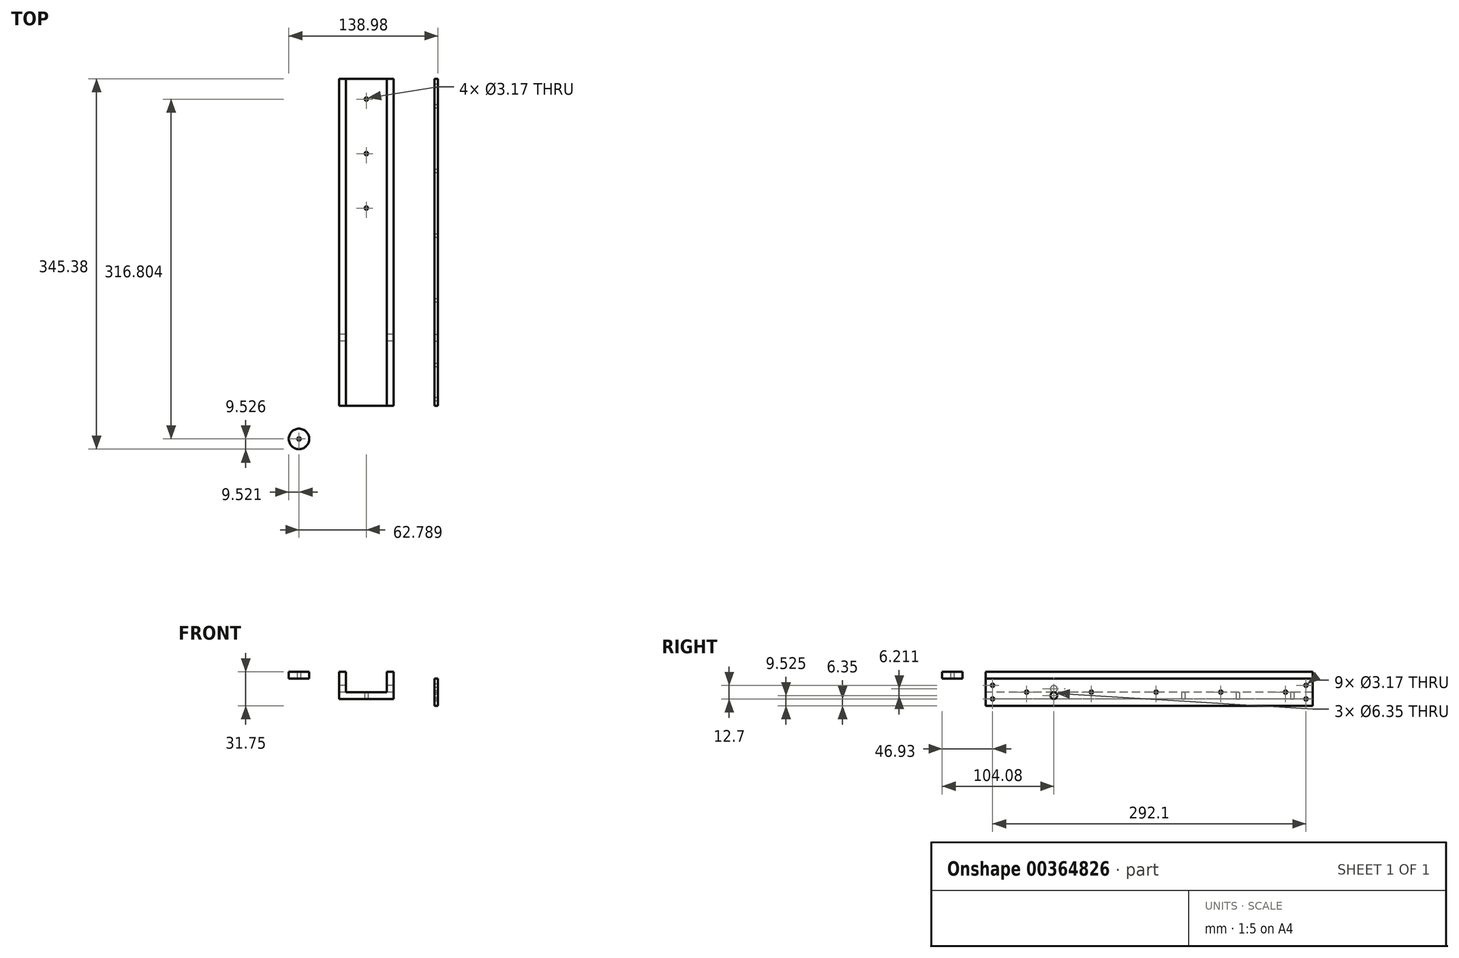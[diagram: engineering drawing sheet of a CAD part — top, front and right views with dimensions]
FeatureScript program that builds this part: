
annotation { "Feature Type Name" : "Feature", "Feature Type Description" : "" }
export const myFeature = defineFeature(function(context is Context, id is Id, definition is map)
    precondition{}
    {
        {
            var Q0;
            Q0=qCreatedBy(makeId("Front.planeOp"),FACE);
            var sketch = newSketch(context, id + "F0", { "sketchPlane" : qUnion([Q0])});
            skLineSegment(sketch, "E0", {"start": v(-25.4, 6.21) * mm, "end": v(-25.4, -19.19) * mm});
            skLineSegment(sketch, "E1", {"start": v(-25.4, -19.19) * mm, "end": v(25.4, -19.19) * mm});
            skLineSegment(sketch, "E2", {"start": v(25.4, -19.19) * mm, "end": v(25.4, 6.21) * mm});
            skLineSegment(sketch, "E3", {"start": v(25.4, 6.21) * mm, "end": v(19.05, 6.21) * mm});
            skLineSegment(sketch, "E4", {"start": v(19.05, 6.21) * mm, "end": v(19.05, -12.84) * mm});
            skLineSegment(sketch, "E5", {"start": v(19.05, -12.84) * mm, "end": v(-19.05, -12.84) * mm});
            skLineSegment(sketch, "E6", {"start": v(-19.05, -12.84) * mm, "end": v(-19.05, 6.21) * mm});
            skLineSegment(sketch, "E7", {"start": v(-19.05, 6.21) * mm, "end": v(-25.4, 6.21) * mm});
            skSolve(sketch);
        }
        {
            var Q0;
            Q0 = qSketchRegion(id + "F0", true);
            extrude(context, id + "F1", {"entities" : qUnion([Q0]), "oppositeDirection" : true, "depth" : 304.8 * mm, "offsetDistance" : 25.4 * mm});
        }
        {
            var Q0;
            Q0=makeQuery(id+"F1.opExtrude","SWEPT_FACE",FACE,{"disambiguationData":[OSD([sQuery(id+"F0.wireOp",EDGE,"E0")])]});
            var sketch = newSketch(context, id + "F2", { "sketchPlane" : qUnion([Q0])});
            skLineSegment(sketch, "E8", {"start": v(2.62, -9.66) * mm, "end": v(-42.46, -9.66) * mm, "construction": true});
            skLineSegment(sketch, "E9", {"start": v(-63.5, -22.2) * mm, "end": v(-63.5, -9.66) * mm, "construction": true});
            skCircle(sketch, "E10", {"center": v(-63.5, -9.66) * mm, "radius": 3.18 * mm});
            skSolve(sketch);
        }
        {
            var Q0;
            Q0 = qSketchRegion(id + "F2", true);
            var Q1;
            Q1=makeQuery(id+"F1.opExtrude","SWEPT_FACE",FACE,{"disambiguationData":[OSD([sQuery(id+"F0.wireOp",EDGE,"E2")])]});
            extrude(context, id + "F3", {"entities" : qUnion([Q0]), "operationType" : NewBodyOperationType.REMOVE, "endBound" : BoundingType.UP_TO_SURFACE, "oppositeDirection" : true, "depth" : 25.4 * mm, "endBoundEntityFace" : qUnion([Q1]), "offsetDistance" : 25.4 * mm});
        }
        {
            var Q0;
            Q0=qCreatedBy(makeId("Top.planeOp"),FACE);
            var sketch = newSketch(context, id + "F4", { "sketchPlane" : qUnion([Q0])});
            skLineSegment(sketch, "E11.bottom", {"start": v(63.5, 0) * mm, "end": v(66.67, 0) * mm});
            skLineSegment(sketch, "E11.top", {"start": v(63.5, 304.8) * mm, "end": v(66.67, 304.8) * mm});
            skLineSegment(sketch, "E11.left", {"start": v(63.5, 0) * mm, "end": v(63.5, 304.8) * mm});
            skLineSegment(sketch, "E11.right", {"start": v(66.67, 0) * mm, "end": v(66.67, 304.8) * mm});
            skSolve(sketch);
        }
        {
            var Q0;
            Q0 = qSketchRegion(id + "F4", true);
            extrude(context, id + "F5", {"entities" : qUnion([Q0]), "oppositeDirection" : true, "depth" : 25.4 * mm, "offsetDistance" : 25.4 * mm});
        }
        {
            var Q0;
            Q0=makeQuery(id+"F5.opExtrude","SWEPT_FACE",FACE,{"disambiguationData":[OSD([sQuery(id+"F4.wireOp",EDGE,"E11.right")])]});
            var sketch = newSketch(context, id + "F6", { "sketchPlane" : qUnion([Q0])});
            skLineSegment(sketch, "E12", {"start": v(-0.34, -15.88) * mm, "end": v(74.66, -15.87) * mm, "construction": true});
            skLineSegment(sketch, "E13", {"start": v(63.5, -28.22) * mm, "end": v(63.5, -15.87) * mm, "construction": true});
            skCircle(sketch, "E14", {"center": v(63.5, -15.87) * mm, "radius": 3.18 * mm});
            skSolve(sketch);
        }
        {
            var Q0;
            Q0 = qSketchRegion(id + "F6", true);
            extrude(context, id + "F7", {"entities" : qUnion([Q0]), "operationType" : NewBodyOperationType.REMOVE, "oppositeDirection" : true, "depth" : 25.4 * mm, "offsetDistance" : 25.4 * mm});
        }
        {
            var Q0;
            Q0=makeQuery(id+"F5.opExtrude","SWEPT_FACE",FACE,{"disambiguationData":[OSD([sQuery(id+"F4.wireOp",EDGE,"E11.right")])]});
            var sketch = newSketch(context, id + "F8", { "sketchPlane" : qUnion([Q0])});
            skLineSegment(sketch, "E15", {"start": v(-6.26, -12.7) * mm, "end": v(309.85, -12.7) * mm, "construction": true});
            skPoint(sketch, "E15.startSnap0", {"position": v(0, -12.7) * mm});
            skLineSegment(sketch, "E16", {"start": v(298.45, -28.77) * mm, "end": v(298.45, 10.49) * mm, "construction": true});
            skLineSegment(sketch, "E17", {"start": v(6.35, -30.25) * mm, "end": v(6.35, 2.85) * mm, "construction": true});
            skLineSegment(sketch, "E18", {"start": v(-5.59, -6.35) * mm, "end": v(6.35, -6.35) * mm, "construction": true});
            skLineSegment(sketch, "E19", {"start": v(-6.94, -19.05) * mm, "end": v(6.35, -19.05) * mm, "construction": true});
            skLineSegment(sketch, "E20", {"start": v(298.45, -6.35) * mm, "end": v(311.24, -6.35) * mm, "construction": true});
            skLineSegment(sketch, "E21", {"start": v(298.45, -19.05) * mm, "end": v(309.9, -19.05) * mm, "construction": true});
            skLineSegment(sketch, "E22", {"start": v(38.1, -3.72) * mm, "end": v(38.1, -12.7) * mm, "construction": true});
            skLineSegment(sketch, "E23", {"start": v(279.4, -4.06) * mm, "end": v(279.4, -12.7) * mm, "construction": true});
            skLineSegment(sketch, "E24", {"start": v(98.43, -4.74) * mm, "end": v(98.43, -12.7) * mm, "construction": true});
            skLineSegment(sketch, "E25", {"start": v(158.75, -6.6) * mm, "end": v(158.75, -12.7) * mm, "construction": true});
            skLineSegment(sketch, "E26", {"start": v(219.07, -5.25) * mm, "end": v(219.07, -12.7) * mm, "construction": true});
            skPoint(sketch, "E27.orphan", {"position": v(15.82, -6.35) * mm});
            skPoint(sketch, "E28.orphan", {"position": v(15.82, -19.05) * mm});
            skPoint(sketch, "E29.orphan", {"position": v(283.42, -6.35) * mm});
            skPoint(sketch, "E30.orphan", {"position": v(282.58, -19.05) * mm});
            skPoint(sketch, "E31.orphan", {"position": v(279.4, -21.15) * mm});
            skPoint(sketch, "E32.orphan", {"position": v(219.07, -19.12) * mm});
            skPoint(sketch, "E33.orphan", {"position": v(158.75, -20.65) * mm});
            skPoint(sketch, "E34.orphan", {"position": v(98.43, -20.65) * mm});
            skPoint(sketch, "E35.orphan", {"position": v(38.1, -21.15) * mm});
            skCircle(sketch, "E36", {"center": v(6.35, -6.35) * mm, "radius": 1.59 * mm});
            skCircle(sketch, "E37", {"center": v(6.35, -19.05) * mm, "radius": 1.59 * mm});
            skCircle(sketch, "E38", {"center": v(38.1, -12.7) * mm, "radius": 1.59 * mm});
            skCircle(sketch, "E39", {"center": v(98.43, -12.7) * mm, "radius": 1.59 * mm});
            skCircle(sketch, "E40", {"center": v(158.75, -12.7) * mm, "radius": 1.59 * mm});
            skCircle(sketch, "E41", {"center": v(219.07, -12.7) * mm, "radius": 1.59 * mm});
            skCircle(sketch, "E42", {"center": v(279.4, -12.7) * mm, "radius": 1.59 * mm});
            skCircle(sketch, "E43", {"center": v(298.45, -6.35) * mm, "radius": 1.59 * mm});
            skCircle(sketch, "E44", {"center": v(298.45, -19.05) * mm, "radius": 1.59 * mm});
            skSolve(sketch);
        }
        {
            var Q0;
            Q0 = qSketchRegion(id + "F8", true);
            extrude(context, id + "F9", {"entities" : qUnion([Q0]), "operationType" : NewBodyOperationType.REMOVE, "oppositeDirection" : true, "depth" : 25.4 * mm, "offsetDistance" : 25.4 * mm});
        }
        {
            var Q0;
            Q0=qCreatedBy(makeId("Top.planeOp"),FACE);
            var sketch = newSketch(context, id + "F10", { "sketchPlane" : qUnion([Q0])});
            skCircle(sketch, "E45", {"center": v(-62.79, -31.05) * mm, "radius": 1.59 * mm});
            skCircle(sketch, "E46", {"center": v(-62.79, -31.05) * mm, "radius": 9.53 * mm});
            skSolve(sketch);
        }
        {
            var Q0;
            Q0 = qSketchRegion(id + "F10", true);
            extrude(context, id + "F11", {"entities" : qUnion([Q0]), "depth" : 6.35 * mm, "offsetDistance" : 25.4 * mm});
        }
        {
            var Q0;
            Q0=makeQuery(id+"F1.opExtrude","SWEPT_FACE",FACE,{"disambiguationData":[OSD([sQuery(id+"F0.wireOp",EDGE,"E1")])]});
            var sketch = newSketch(context, id + "F12", { "sketchPlane" : qUnion([Q0])});
            skLineSegment(sketch, "E47", {"start": v(0, -317.18) * mm, "end": v(0, -36.39) * mm, "construction": true});
            skPoint(sketch, "E47.startSnap0", {"position": v(0, -304.8) * mm});
            skLineSegment(sketch, "E48", {"start": v(0, -285.75) * mm, "end": v(-14.67, -285.75) * mm, "construction": true});
            skLineSegment(sketch, "E49", {"start": v(0, -234.95) * mm, "end": v(-16.38, -234.95) * mm, "construction": true});
            skLineSegment(sketch, "E50", {"start": v(0, -184.15) * mm, "end": v(-14.29, -184.15) * mm, "construction": true});
            skCircle(sketch, "E51", {"center": v(0, -184.15) * mm, "radius": 1.59 * mm});
            skCircle(sketch, "E52", {"center": v(0, -234.95) * mm, "radius": 1.59 * mm});
            skCircle(sketch, "E53", {"center": v(0, -285.75) * mm, "radius": 1.59 * mm});
            skSolve(sketch);
        }
        {
            var Q0;
            Q0 = qSketchRegion(id + "F12", true);
            extrude(context, id + "F13", {"entities" : qUnion([Q0]), "operationType" : NewBodyOperationType.REMOVE, "oppositeDirection" : true, "depth" : 25.4 * mm, "offsetDistance" : 25.4 * mm});
        }
    });
